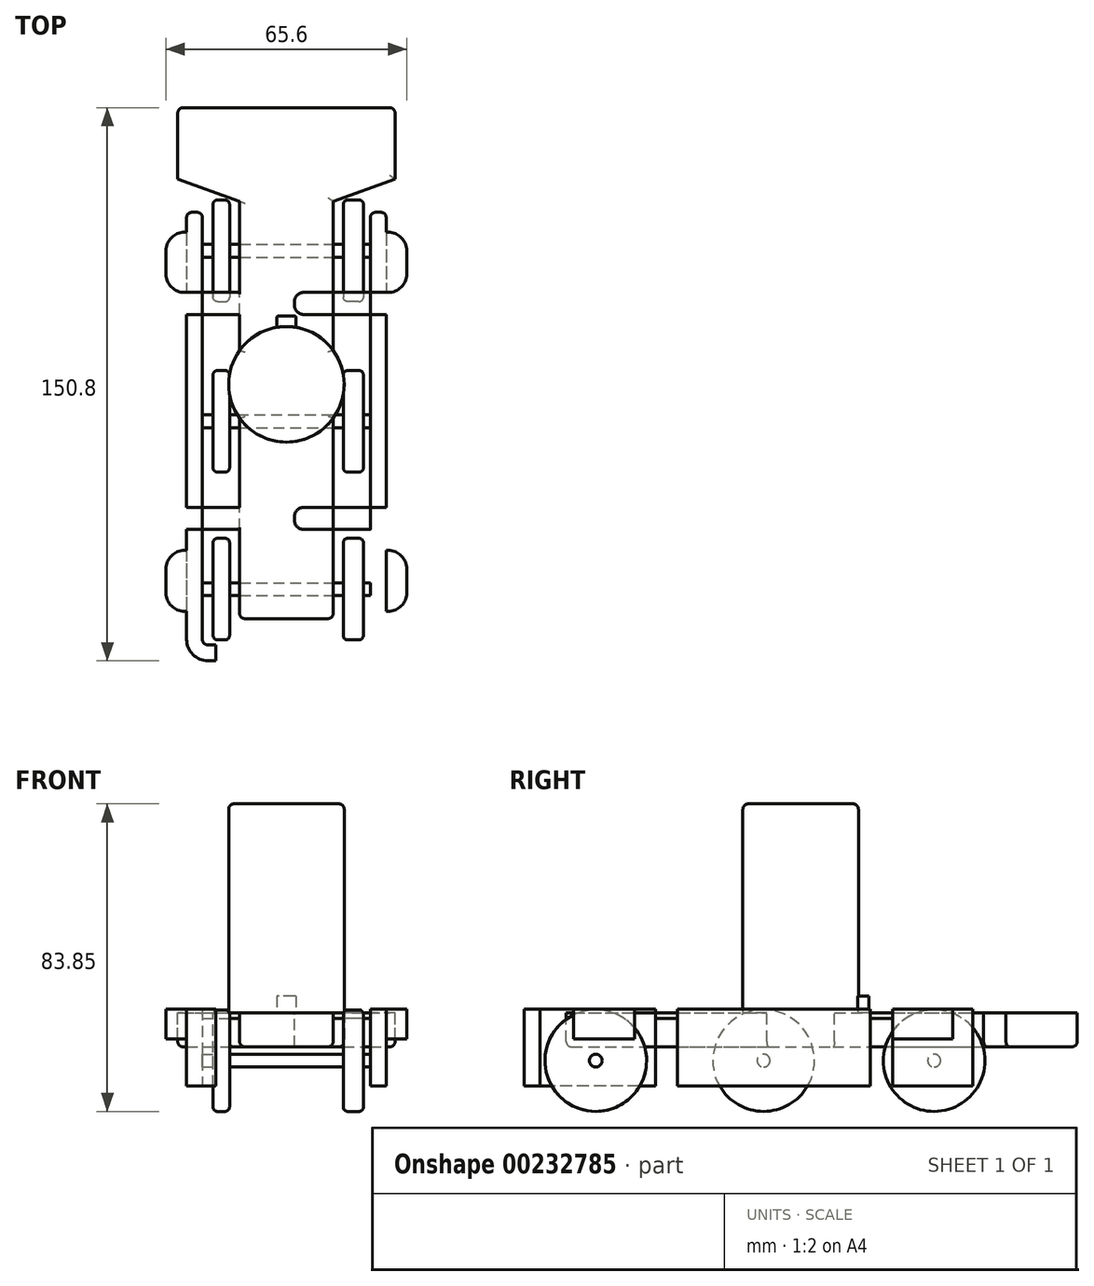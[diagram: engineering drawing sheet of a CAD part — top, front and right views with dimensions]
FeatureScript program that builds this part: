
annotation { "Feature Type Name" : "Feature", "Feature Type Description" : "" }
export const myFeature = defineFeature(function(context is Context, id is Id, definition is map)
    precondition{}
    {
        {
            var Q0;
            Q0=qCreatedBy(makeId("Top.planeOp"),FACE);
            var sketch = newSketch(context, id + "F0", { "sketchPlane" : qUnion([Q0])});
            skLineSegment(sketch, "E0.bottom", {"start": v(0, 75.4) * mm, "end": v(-29.63, 75.4) * mm});
            skLineSegment(sketch, "E0.top", {"start": v(-19.2, -75.4) * mm, "end": v(-21.33, -75.4) * mm});
            skLineSegment(sketch, "E0.right", {"start": v(-27.2, 46.9) * mm, "end": v(-27.2, -69.53) * mm});
            skPoint(sketch, "E0.middle", {"position": v(0, 0) * mm});
            skCircle(sketch, "E1", {"center": v(0, 0) * mm, "radius": 15.75 * mm});
            skLineSegment(sketch, "E2.bottom", {"start": v(2.65, 18.6) * mm, "end": v(-2.65, 18.6) * mm});
            skLineSegment(sketch, "E2.left", {"start": v(2.65, 18.6) * mm, "end": v(2.65, 15.53) * mm});
            skLineSegment(sketch, "E2.right", {"start": v(-2.65, 18.6) * mm, "end": v(-2.65, 15.53) * mm});
            skPoint(sketch, "E2.middle", {"position": v(0, 16.85) * mm});
            skPoint(sketch, "E3.orphan", {"position": v(-2.65, 15.1) * mm});
            skPoint(sketch, "E4.orphan", {"position": v(2.65, 15.1) * mm});
            skLineSegment(sketch, "E5.0", {"start": v(-19.2, -71.1) * mm, "end": v(-21.33, -71.1) * mm});
            skLineSegment(sketch, "E5.1", {"start": v(-22.9, 46.9) * mm, "end": v(-22.9, -69.53) * mm});
            skLineSegment(sketch, "E6", {"start": v(-27.2, 46.9) * mm, "end": v(-22.9, 46.9) * mm});
            skLineSegment(sketch, "E7", {"start": v(-19.2, -71.1) * mm, "end": v(-19.2, -75.4) * mm});
            skPoint(sketch, "E8.visualSharp", {"position": v(-22.9, -71.1) * mm});
            skArc(sketch, "E8.filletArc", {"start": v(-22.9, -69.53) * mm, "mid": v(-22.44, -70.64) * mm, "end": v(-21.33, -71.1) * mm});
            skArc(sketch, "E9.0", {"start": v(-27.2, -69.53) * mm, "mid": v(-25.48, -73.68) * mm, "end": v(-21.33, -75.4) * mm});
            skPoint(sketch, "E10.orphan", {"position": v(-27.2, -75.4) * mm});
            skLineSegment(sketch, "E11.top", {"start": v(-12.75, -63.9) * mm, "end": v(0, -63.9) * mm});
            skLineSegment(sketch, "E12.bottom", {"start": v(-27.2, -39.58) * mm, "end": v(-4.7, -39.58) * mm});
            skLineSegment(sketch, "E12.top", {"start": v(-27.2, -33.58) * mm, "end": v(-4.7, -33.58) * mm});
            skLineSegment(sketch, "E12.left", {"start": v(-27.2, -39.58) * mm, "end": v(-27.2, -33.58) * mm});
            skLineSegment(sketch, "E12.right", {"start": v(-2.2, -37.08) * mm, "end": v(-2.2, -36.08) * mm});
            skPoint(sketch, "E13.visualSharp", {"position": v(-2.2, -33.58) * mm});
            skArc(sketch, "E13.filletArc", {"start": v(-2.2, -36.08) * mm, "mid": v(-2.93, -34.3) * mm, "end": v(-4.7, -33.58) * mm});
            skPoint(sketch, "E14.visualSharp", {"position": v(-2.2, -39.58) * mm});
            skArc(sketch, "E14.filletArc", {"start": v(-4.7, -39.58) * mm, "mid": v(-2.93, -38.84) * mm, "end": v(-2.2, -37.08) * mm});
            skLineSegment(sketch, "E15", {"start": v(-29.63, 56) * mm, "end": v(-12.75, 49.9) * mm});
            skPoint(sketch, "E16", {"position": v(0, 75.4) * mm});
            skPoint(sketch, "E17", {"position": v(0, -63.9) * mm});
            skLineSegment(sketch, "E18", {"start": v(-29.63, 56) * mm, "end": v(-29.63, 75.4) * mm});
            skLineSegment(sketch, "E19", {"start": v(-12.75, -63.9) * mm, "end": v(-12.75, 49.9) * mm});
            skLineSegment(sketch, "E20.bottom", {"start": v(-27.2, 19.04) * mm, "end": v(-4.7, 19.04) * mm});
            skLineSegment(sketch, "E20.top", {"start": v(-27.2, 25.04) * mm, "end": v(-4.7, 25.04) * mm});
            skLineSegment(sketch, "E20.left", {"start": v(-27.2, 19.04) * mm, "end": v(-27.2, 25.04) * mm});
            skLineSegment(sketch, "E20.right", {"start": v(-2.2, 21.54) * mm, "end": v(-2.2, 22.54) * mm});
            skPoint(sketch, "E21.visualSharp", {"position": v(-2.2, 25.04) * mm});
            skArc(sketch, "E21.filletArc", {"start": v(-2.2, 22.54) * mm, "mid": v(-2.93, 24.31) * mm, "end": v(-4.7, 25.04) * mm});
            skPoint(sketch, "E22.visualSharp", {"position": v(-2.2, 19.04) * mm});
            skArc(sketch, "E22.filletArc", {"start": v(-4.7, 19.04) * mm, "mid": v(-2.93, 19.78) * mm, "end": v(-2.2, 21.54) * mm});
            skLineSegment(sketch, "E23.bottom", {"start": v(-32.8, 82.4) * mm, "end": v(32.8, 82.4) * mm, "construction": true});
            skLineSegment(sketch, "E23.top", {"start": v(-32.8, -82.4) * mm, "end": v(32.8, -82.4) * mm, "construction": true});
            skLineSegment(sketch, "E23.right", {"start": v(32.8, 82.4) * mm, "end": v(32.8, -82.4) * mm, "construction": true});
            skLineSegment(sketch, "E24.bottom", {"start": v(-32.8, -45.3) * mm, "end": v(-27.2, -45.3) * mm});
            skLineSegment(sketch, "E24.top", {"start": v(-32.8, -61.9) * mm, "end": v(-27.2, -61.9) * mm});
            skLineSegment(sketch, "E24.left", {"start": v(-32.8, -45.3) * mm, "end": v(-32.8, -61.9) * mm});
            skLineSegment(sketch, "E24.right", {"start": v(-27.2, -45.3) * mm, "end": v(-27.2, -61.9) * mm});
            skLineSegment(sketch, "E25.bottom", {"start": v(-32.8, 25.04) * mm, "end": v(-27.2, 25.04) * mm});
            skLineSegment(sketch, "E25.top", {"start": v(-32.8, 41.44) * mm, "end": v(-27.2, 41.44) * mm});
            skLineSegment(sketch, "E25.left", {"start": v(-32.8, 25.04) * mm, "end": v(-32.8, 41.44) * mm});
            skLineSegment(sketch, "E25.right", {"start": v(-27.2, 25.04) * mm, "end": v(-27.2, 41.44) * mm});
            skArc(sketch, "E26.MirrorCS", {"start": v(2.2, -36.08) * mm, "mid": v(2.93, -34.3) * mm, "end": v(4.7, -33.58) * mm});
            skLineSegment(sketch, "E27.MirrorCS", {"start": v(2.2, -37.08) * mm, "end": v(2.2, -36.08) * mm});
            skArc(sketch, "E28.MirrorCS", {"start": v(4.7, -39.58) * mm, "mid": v(2.93, -38.84) * mm, "end": v(2.2, -37.08) * mm});
            skArc(sketch, "E29.MirrorCS", {"start": v(4.7, 19.04) * mm, "mid": v(2.93, 19.78) * mm, "end": v(2.2, 21.54) * mm});
            skLineSegment(sketch, "E30.MirrorCS", {"start": v(2.2, 21.54) * mm, "end": v(2.2, 22.54) * mm});
            skArc(sketch, "E31.MirrorCS", {"start": v(2.2, 22.54) * mm, "mid": v(2.93, 24.31) * mm, "end": v(4.7, 25.04) * mm});
            skArc(sketch, "E32.MirrorCS", {"start": v(22.9, -69.53) * mm, "mid": v(22.44, -70.64) * mm, "end": v(21.33, -71.1) * mm});
            skLineSegment(sketch, "E33.MirrorCS", {"start": v(19.2, -75.4) * mm, "end": v(21.33, -75.4) * mm});
            skLineSegment(sketch, "E34.MirrorCS", {"start": v(19.2, -71.1) * mm, "end": v(21.33, -71.1) * mm});
            skLineSegment(sketch, "E35.MirrorCS", {"start": v(27.2, -45.3) * mm, "end": v(27.2, -61.9) * mm});
            skLineSegment(sketch, "E36.MirrorCS", {"start": v(32.8, -45.3) * mm, "end": v(32.8, -61.9) * mm});
            skLineSegment(sketch, "E37.MirrorCS", {"start": v(32.8, 25.04) * mm, "end": v(32.8, 41.44) * mm});
            skPoint(sketch, "E38.MirrorP", {"position": v(22.9, -71.1) * mm});
            skLineSegment(sketch, "E39.MirrorCS", {"start": v(27.2, 46.9) * mm, "end": v(27.2, -69.53) * mm});
            skPoint(sketch, "E40.MirrorP", {"position": v(27.2, -75.4) * mm});
            skArc(sketch, "E41.MirrorCS", {"start": v(27.2, -69.53) * mm, "mid": v(25.48, -73.68) * mm, "end": v(21.33, -75.4) * mm});
            skLineSegment(sketch, "E42.MirrorCS", {"start": v(27.2, 46.9) * mm, "end": v(22.9, 46.9) * mm});
            skLineSegment(sketch, "E43.MirrorCS", {"start": v(32.8, -45.3) * mm, "end": v(27.2, -45.3) * mm});
            skLineSegment(sketch, "E44.MirrorCS", {"start": v(27.2, 19.04) * mm, "end": v(27.2, 25.04) * mm});
            skLineSegment(sketch, "E45.MirrorCS", {"start": v(27.2, -39.58) * mm, "end": v(4.7, -39.58) * mm});
            skLineSegment(sketch, "E46.MirrorCS", {"start": v(22.9, 46.9) * mm, "end": v(22.9, -69.53) * mm});
            skLineSegment(sketch, "E47.MirrorCS", {"start": v(32.8, 41.44) * mm, "end": v(27.2, 41.44) * mm});
            skLineSegment(sketch, "E48.MirrorCS", {"start": v(32.8, 25.04) * mm, "end": v(27.2, 25.04) * mm});
            skLineSegment(sketch, "E49.MirrorCS", {"start": v(27.2, 19.04) * mm, "end": v(4.7, 19.04) * mm});
            skLineSegment(sketch, "E50.MirrorCS", {"start": v(27.2, -39.58) * mm, "end": v(27.2, -33.58) * mm});
            skLineSegment(sketch, "E51.MirrorCS", {"start": v(19.2, -71.1) * mm, "end": v(19.2, -75.4) * mm});
            skLineSegment(sketch, "E52.MirrorCS", {"start": v(27.2, -33.58) * mm, "end": v(4.7, -33.58) * mm});
            skLineSegment(sketch, "E53.MirrorCS", {"start": v(32.8, -61.9) * mm, "end": v(27.2, -61.9) * mm});
            skLineSegment(sketch, "E54.MirrorCS", {"start": v(27.2, 25.04) * mm, "end": v(4.7, 25.04) * mm});
            skLineSegment(sketch, "E55.MirrorCS", {"start": v(27.2, 25.04) * mm, "end": v(27.2, 41.44) * mm});
            skLineSegment(sketch, "E56.MirrorCS", {"start": v(12.75, -63.9) * mm, "end": v(0, -63.9) * mm});
            skLineSegment(sketch, "E57.MirrorCS", {"start": v(12.75, -63.9) * mm, "end": v(12.75, 49.9) * mm});
            skLineSegment(sketch, "E58.MirrorCS", {"start": v(29.63, 56) * mm, "end": v(12.75, 49.9) * mm});
            skLineSegment(sketch, "E59.MirrorCS", {"start": v(0, 75.4) * mm, "end": v(29.63, 75.4) * mm});
            skLineSegment(sketch, "E60.MirrorCS", {"start": v(29.63, 56) * mm, "end": v(29.63, 75.4) * mm});
            skSolve(sketch);
        }
        {
            var Q0;
            Q0=makeQuery(id+"F0.imprint","IMPRINT",FACE,{"disambiguationData":[TD([[makeQuery(id+"F0.imprint","IMPRINT",EDGE,{"derivedFrom":sQuery(id+"F0.wireOp",EDGE,"E0.bottom")}),1.0]])]});
            var Q1;
            {var subQ4=sQuery(id+"F0.wireOp",EDGE,"E26.MirrorCS");Q1=makeQuery(id+"F0.imprint","IMPRINT",FACE,{"disambiguationData":[TD([[makeQuery(id+"F0.imprint","IMPRINT",EDGE,{"derivedFrom":subQ4}),-1.0]])]});}
            var Q2;
            {var subQ9=sQuery(id+"F0.wireOp",EDGE,"E11.top");Q2=makeQuery(id+"F0.imprint","IMPRINT",FACE,{"disambiguationData":[TD([[makeQuery(id+"F0.imprint","IMPRINT",EDGE,{"derivedFrom":subQ9}),1.0]])]});}
            var Q3;
            Q3=makeQuery(id+"F0.imprint","IMPRINT",FACE,{"disambiguationData":[TD([[makeQuery(id+"F0.imprint","IMPRINT",EDGE,{"derivedFrom":sQuery(id+"F0.wireOp",EDGE,"E12.right")}),1.0]])]});
            var Q4;
            {var subQ1=sQuery(id+"F0.wireOp",EDGE,"E29.MirrorCS");Q4=makeQuery(id+"F0.imprint","IMPRINT",FACE,{"disambiguationData":[TD([[makeQuery(id+"F0.imprint","IMPRINT",EDGE,{"derivedFrom":subQ1}),-1.0]])]});}
            var Q5;
            Q5=makeQuery(id+"F0.imprint","IMPRINT",FACE,{"disambiguationData":[TD([[makeQuery(id+"F0.imprint","IMPRINT",EDGE,{"derivedFrom":sQuery(id+"F0.wireOp",EDGE,"E20.right")}),1.0]])]});
            extrude(context, id + "F1", {"entities" : qUnion([Q0, Q1, Q2, Q3, Q4, Q5]), "oppositeDirection" : true, "depth" : 7.75 * mm});
        }
        {
            var Q0;
            {var subQ1=sQuery(id+"F0.wireOp",EDGE,"E1");var subQ7=makeQuery(id+"F0.imprint","INTERSECT",VERTEX,{"derivedFrom":[subQ1,sQuery(id+"F0.wireOp",EDGE,"E2.left")]});Q0=makeQuery(id+"F0.imprint","IMPRINT",FACE,{"disambiguationData":[TD([[makeQuery(id+"F0.imprint","IMPRINT",EDGE,{"disambiguationData":[TD([[subQ7,1.0]])],"derivedFrom":subQ1}),1.0]])]});}
            var Q1;
            {var subQ0=sQuery(id+"F0.wireOp",EDGE,"E19");var subQ1=sQuery(id+"F0.wireOp",EDGE,"E1");var subQ2=makeQuery(id+"F0.imprint","INTERSECT",VERTEX,{"disambiguationData":[OD(0.0)],"derivedFrom":[subQ1,subQ0]});Q1=makeQuery(id+"F0.imprint","IMPRINT",FACE,{"disambiguationData":[TD([[makeQuery(id+"F0.imprint","IMPRINT",EDGE,{"disambiguationData":[TD([[subQ2,-1.0]])],"derivedFrom":subQ1}),1.0]])]});}
            var Q2;
            {var subQ0=sQuery(id+"F0.wireOp",EDGE,"E57.MirrorCS");var subQ1=sQuery(id+"F0.wireOp",EDGE,"E1");var subQ2=makeQuery(id+"F0.imprint","INTERSECT",VERTEX,{"disambiguationData":[OD(0.0)],"derivedFrom":[subQ1,subQ0]});Q2=makeQuery(id+"F0.imprint","IMPRINT",FACE,{"disambiguationData":[TD([[makeQuery(id+"F0.imprint","IMPRINT",EDGE,{"disambiguationData":[TD([[subQ2,1.0]])],"derivedFrom":subQ1}),1.0]])]});}
            var Q3;
            Q3=makeQuery(id+"F1.opExtrude","CAP_FACE",FACE,{"disambiguationData":[OSD([sQuery(id+"F0.wireOp",EDGE,"E1"),sQuery(id+"F0.wireOp",EDGE,"E11.top"),sQuery(id+"F0.wireOp",EDGE,"E19"),sQuery(id+"F0.wireOp",EDGE,"E56.MirrorCS"),sQuery(id+"F0.wireOp",EDGE,"E57.MirrorCS")])],"isStart":false});
            extrude(context, id + "F2", {"entities" : qUnion([Q0, Q1, Q2]), "operationType" : NewBodyOperationType.ADD, "depth" : 58.5 * mm, "hasSecondDirection" : true, "secondDirectionBound" : SecondDirectionBoundingType.UP_TO_SURFACE, "secondDirectionOppositeDirection" : true, "secondDirectionBoundEntityFace" : qUnion([Q3]), "secondDirectionDepth" : 25 * mm});
        }
        {
            var Q0;
            Q0=makeQuery(id+"F0.imprint","IMPRINT",FACE,{"disambiguationData":[TD([[makeQuery(id+"F0.imprint","IMPRINT",EDGE,{"derivedFrom":sQuery(id+"F0.wireOp",EDGE,"E2.bottom")}),1.0]])]});
            var Q1;
            Q1=makeQuery(id+"F1.opExtrude","CAP_FACE",FACE,{"disambiguationData":[OSD([sQuery(id+"F0.wireOp",EDGE,"E0.bottom"),sQuery(id+"F0.wireOp",EDGE,"E1"),sQuery(id+"F0.wireOp",EDGE,"E2.bottom"),sQuery(id+"F0.wireOp",EDGE,"E2.left"),sQuery(id+"F0.wireOp",EDGE,"E2.right"),sQuery(id+"F0.wireOp",EDGE,"E15"),sQuery(id+"F0.wireOp",EDGE,"E18"),sQuery(id+"F0.wireOp",EDGE,"E19"),sQuery(id+"F0.wireOp",EDGE,"E57.MirrorCS"),sQuery(id+"F0.wireOp",EDGE,"E58.MirrorCS"),sQuery(id+"F0.wireOp",EDGE,"E59.MirrorCS"),sQuery(id+"F0.wireOp",EDGE,"E60.MirrorCS")])],"isStart":false});
            extrude(context, id + "F3", {"entities" : qUnion([Q0]), "operationType" : NewBodyOperationType.ADD, "depth" : 6.1 * mm, "hasSecondDirection" : true, "secondDirectionBound" : SecondDirectionBoundingType.UP_TO_SURFACE, "secondDirectionOppositeDirection" : true, "secondDirectionBoundEntityFace" : qUnion([Q1]), "secondDirectionDepth" : 25 * mm});
        }
        {
            var Q0;
            {var subQ7=sQuery(id+"F0.wireOp",EDGE,"E32.MirrorCS");Q0=makeQuery(id+"F0.imprint","IMPRINT",FACE,{"disambiguationData":[TD([[makeQuery(id+"F0.imprint","IMPRINT",EDGE,{"derivedFrom":subQ7}),1.0]])]});}
            var Q1;
            {var subQ0=sQuery(id+"F0.wireOp",EDGE,"E50.MirrorCS");Q1=makeQuery(id+"F0.imprint","IMPRINT",FACE,{"disambiguationData":[TD([[makeQuery(id+"F0.imprint","IMPRINT",EDGE,{"derivedFrom":subQ0}),1.0]])]});}
            var Q2;
            {var subQ0=sQuery(id+"F0.wireOp",EDGE,"E49.MirrorCS");var subQ5=sQuery(id+"F0.wireOp",EDGE,"E46.MirrorCS");var subQ6=makeQuery(id+"F0.imprint","INTERSECT",VERTEX,{"derivedFrom":[subQ5,subQ0]});Q2=makeQuery(id+"F0.imprint","IMPRINT",FACE,{"disambiguationData":[TD([[makeQuery(id+"F0.imprint","IMPRINT",EDGE,{"disambiguationData":[TD([[subQ6,-1.0]])],"derivedFrom":subQ5}),1.0]])]});}
            var Q3;
            {var subQ5=sQuery(id+"F0.wireOp",EDGE,"E44.MirrorCS");Q3=makeQuery(id+"F0.imprint","IMPRINT",FACE,{"disambiguationData":[TD([[makeQuery(id+"F0.imprint","IMPRINT",EDGE,{"derivedFrom":subQ5}),1.0]])]});}
            var Q4;
            {var subQ7=sQuery(id+"F0.wireOp",EDGE,"E42.MirrorCS");Q4=makeQuery(id+"F0.imprint","IMPRINT",FACE,{"disambiguationData":[TD([[makeQuery(id+"F0.imprint","IMPRINT",EDGE,{"derivedFrom":subQ7}),1.0]])]});}
            var Q5;
            {var subQ0=sQuery(id+"F0.wireOp",EDGE,"E6");Q5=makeQuery(id+"F0.imprint","IMPRINT",FACE,{"disambiguationData":[TD([[makeQuery(id+"F0.imprint","IMPRINT",EDGE,{"derivedFrom":subQ0}),-1.0]])]});}
            var Q6;
            {var subQ3=sQuery(id+"F0.wireOp",EDGE,"E20.bottom");var subQ5=sQuery(id+"F0.wireOp",EDGE,"E5.1");var subQ6=makeQuery(id+"F0.imprint","INTERSECT",VERTEX,{"derivedFrom":[subQ5,subQ3]});Q6=makeQuery(id+"F0.imprint","IMPRINT",FACE,{"disambiguationData":[TD([[makeQuery(id+"F0.imprint","IMPRINT",EDGE,{"disambiguationData":[TD([[subQ6,-1.0]])],"derivedFrom":subQ5}),-1.0]])]});}
            var Q7;
            {var subQ0=sQuery(id+"F0.wireOp",EDGE,"E20.left");Q7=makeQuery(id+"F0.imprint","IMPRINT",FACE,{"disambiguationData":[TD([[makeQuery(id+"F0.imprint","IMPRINT",EDGE,{"derivedFrom":subQ0}),-1.0]])]});}
            var Q8;
            {var subQ5=sQuery(id+"F0.wireOp",EDGE,"E12.left");Q8=makeQuery(id+"F0.imprint","IMPRINT",FACE,{"disambiguationData":[TD([[makeQuery(id+"F0.imprint","IMPRINT",EDGE,{"derivedFrom":subQ5}),-1.0]])]});}
            var Q9;
            Q9=makeQuery(id+"F0.imprint","IMPRINT",FACE,{"disambiguationData":[TD([[makeQuery(id+"F0.imprint","IMPRINT",EDGE,{"derivedFrom":sQuery(id+"F0.wireOp",EDGE,"E0.top")}),-1.0]])]});
            extrude(context, id + "F4", {"entities" : qUnion([Q0, Q1, Q2, Q3, Q4, Q5, Q6, Q7, Q8, Q9]), "operationType" : NewBodyOperationType.ADD, "depth" : 2.54 * mm, "hasSecondDirection" : true, "secondDirectionOppositeDirection" : true, "secondDirectionDepth" : 18.46 * mm});
        }
        {
            var Q0;
            Q0=makeQuery(id+"F0.imprint","IMPRINT",FACE,{"disambiguationData":[TD([[makeQuery(id+"F0.imprint","IMPRINT",EDGE,{"derivedFrom":sQuery(id+"F0.wireOp",EDGE,"E37.MirrorCS")}),1.0]])]});
            var Q1;
            Q1=makeQuery(id+"F0.imprint","IMPRINT",FACE,{"disambiguationData":[TD([[makeQuery(id+"F0.imprint","IMPRINT",EDGE,{"derivedFrom":sQuery(id+"F0.wireOp",EDGE,"E36.MirrorCS")}),-1.0]])]});
            var Q2;
            Q2=makeQuery(id+"F0.imprint","IMPRINT",FACE,{"disambiguationData":[TD([[makeQuery(id+"F0.imprint","IMPRINT",EDGE,{"derivedFrom":sQuery(id+"F0.wireOp",EDGE,"E24.bottom")}),-1.0]])]});
            var Q3;
            {var subQ2=sQuery(id+"F0.wireOp",EDGE,"E25.bottom");Q3=makeQuery(id+"F0.imprint","IMPRINT",FACE,{"disambiguationData":[TD([[makeQuery(id+"F0.imprint","IMPRINT",EDGE,{"derivedFrom":subQ2}),1.0]])]});}
            var Q4;
            Q4=makeQuery(id+"F4.opExtrude","CAP_FACE",FACE,{"disambiguationData":[OSD([sQuery(id+"F0.wireOp",EDGE,"E32.MirrorCS"),sQuery(id+"F0.wireOp",EDGE,"E33.MirrorCS"),sQuery(id+"F0.wireOp",EDGE,"E34.MirrorCS"),sQuery(id+"F0.wireOp",EDGE,"E39.MirrorCS"),sQuery(id+"F0.wireOp",EDGE,"E41.MirrorCS"),sQuery(id+"F0.wireOp",EDGE,"E42.MirrorCS"),sQuery(id+"F0.wireOp",EDGE,"E44.MirrorCS"),sQuery(id+"F0.wireOp",EDGE,"E46.MirrorCS"),sQuery(id+"F0.wireOp",EDGE,"E50.MirrorCS"),sQuery(id+"F0.wireOp",EDGE,"E51.MirrorCS"),sQuery(id+"F0.wireOp",EDGE,"E55.MirrorCS")])],"isStart":false});
            extrude(context, id + "F5", {"entities" : qUnion([Q0, Q1, Q2, Q3]), "operationType" : NewBodyOperationType.ADD, "endBound" : BoundingType.UP_TO_SURFACE, "endBoundEntityFace" : qUnion([Q4]), "depth" : 5.6 * mm, "hasSecondDirection" : true, "secondDirectionOppositeDirection" : true, "secondDirectionDepth" : 5.6 * mm});
        }
        {
            var Q0;
            {var subQ0=sQuery(id+"F0.wireOp",EDGE,"E12.bottom");var subQ1=sQuery(id+"F0.wireOp",EDGE,"E5.1");var subQ2=makeQuery(id+"F0.imprint","INTERSECT",VERTEX,{"derivedFrom":[subQ1,subQ0]});Q0=makeQuery(id+"F0.imprint","IMPRINT",FACE,{"disambiguationData":[TD([[makeQuery(id+"F0.imprint","IMPRINT",EDGE,{"disambiguationData":[TD([[subQ2,1.0]])],"derivedFrom":subQ1}),1.0]])]});}
            var Q1;
            Q1=makeQuery(id+"F0.imprint","IMPRINT",FACE,{"disambiguationData":[TD([[makeQuery(id+"F0.imprint","IMPRINT",EDGE,{"derivedFrom":sQuery(id+"F0.wireOp",EDGE,"E12.right")}),1.0]])]});
            var Q2;
            {var subQ4=sQuery(id+"F0.wireOp",EDGE,"E26.MirrorCS");Q2=makeQuery(id+"F0.imprint","IMPRINT",FACE,{"disambiguationData":[TD([[makeQuery(id+"F0.imprint","IMPRINT",EDGE,{"derivedFrom":subQ4}),-1.0]])]});}
            var Q3;
            {var subQ0=sQuery(id+"F0.wireOp",EDGE,"E46.MirrorCS");var subQ1=sQuery(id+"F0.wireOp",EDGE,"E45.MirrorCS");var subQ2=makeQuery(id+"F0.imprint","INTERSECT",VERTEX,{"derivedFrom":[subQ1,subQ0]});Q3=makeQuery(id+"F0.imprint","IMPRINT",FACE,{"disambiguationData":[TD([[makeQuery(id+"F0.imprint","IMPRINT",EDGE,{"disambiguationData":[TD([[subQ2,-1.0]])],"derivedFrom":subQ1}),-1.0]])]});}
            var Q4;
            {var subQ0=sQuery(id+"F0.wireOp",EDGE,"E54.MirrorCS");var subQ1=sQuery(id+"F0.wireOp",EDGE,"E46.MirrorCS");var subQ2=makeQuery(id+"F0.imprint","INTERSECT",VERTEX,{"derivedFrom":[subQ1,subQ0]});Q4=makeQuery(id+"F0.imprint","IMPRINT",FACE,{"disambiguationData":[TD([[makeQuery(id+"F0.imprint","IMPRINT",EDGE,{"disambiguationData":[TD([[subQ2,-1.0]])],"derivedFrom":subQ1}),-1.0]])]});}
            var Q5;
            {var subQ1=sQuery(id+"F0.wireOp",EDGE,"E29.MirrorCS");Q5=makeQuery(id+"F0.imprint","IMPRINT",FACE,{"disambiguationData":[TD([[makeQuery(id+"F0.imprint","IMPRINT",EDGE,{"derivedFrom":subQ1}),-1.0]])]});}
            var Q6;
            Q6=makeQuery(id+"F0.imprint","IMPRINT",FACE,{"disambiguationData":[TD([[makeQuery(id+"F0.imprint","IMPRINT",EDGE,{"derivedFrom":sQuery(id+"F0.wireOp",EDGE,"E20.right")}),1.0]])]});
            var Q7;
            {var subQ0=sQuery(id+"F0.wireOp",EDGE,"E20.top");var subQ1=sQuery(id+"F0.wireOp",EDGE,"E5.1");var subQ2=makeQuery(id+"F0.imprint","INTERSECT",VERTEX,{"derivedFrom":[subQ1,subQ0]});Q7=makeQuery(id+"F0.imprint","IMPRINT",FACE,{"disambiguationData":[TD([[makeQuery(id+"F0.imprint","IMPRINT",EDGE,{"disambiguationData":[TD([[subQ2,-1.0]])],"derivedFrom":subQ1}),1.0]])]});}
            var Q8;
            {var subQ0=sQuery(id+"F0.wireOp",EDGE,"E55.MirrorCS");var subQ1=sQuery(id+"F0.wireOp",EDGE,"E39.MirrorCS");Q8=makeQuery(id+"F5.boolean.opBoolean","MERGE",FACE,{"derivedFrom":[makeQuery(id+"F4.opExtrude","CAP_FACE",FACE,{"disambiguationData":[OSD([sQuery(id+"F0.wireOp",EDGE,"E32.MirrorCS"),sQuery(id+"F0.wireOp",EDGE,"E33.MirrorCS"),sQuery(id+"F0.wireOp",EDGE,"E34.MirrorCS"),subQ1,sQuery(id+"F0.wireOp",EDGE,"E41.MirrorCS"),sQuery(id+"F0.wireOp",EDGE,"E42.MirrorCS"),sQuery(id+"F0.wireOp",EDGE,"E44.MirrorCS"),sQuery(id+"F0.wireOp",EDGE,"E46.MirrorCS"),sQuery(id+"F0.wireOp",EDGE,"E50.MirrorCS"),sQuery(id+"F0.wireOp",EDGE,"E51.MirrorCS"),subQ0])],"isStart":false}),makeQuery(id+"F5.opExtrude","CAP_FACE",FACE,{"disambiguationData":[OSD([sQuery(id+"F0.wireOp",EDGE,"E36.MirrorCS"),subQ1,sQuery(id+"F0.wireOp",EDGE,"E43.MirrorCS"),sQuery(id+"F0.wireOp",EDGE,"E53.MirrorCS")])],"isStart":false}),makeQuery(id+"F5.opExtrude","CAP_FACE",FACE,{"disambiguationData":[OSD([sQuery(id+"F0.wireOp",EDGE,"E37.MirrorCS"),sQuery(id+"F0.wireOp",EDGE,"E47.MirrorCS"),sQuery(id+"F0.wireOp",EDGE,"E48.MirrorCS"),subQ0])],"isStart":false})]});}
            var Q9;
            Q9=makeQuery(id+"F1.opExtrude","CAP_FACE",FACE,{"disambiguationData":[OSD([sQuery(id+"F0.wireOp",EDGE,"E1"),sQuery(id+"F0.wireOp",EDGE,"E11.top"),sQuery(id+"F0.wireOp",EDGE,"E19"),sQuery(id+"F0.wireOp",EDGE,"E56.MirrorCS"),sQuery(id+"F0.wireOp",EDGE,"E57.MirrorCS")])],"isStart":true});
            extrude(context, id + "F6", {"entities" : qUnion([Q0, Q1, Q2, Q3, Q4, Q5, Q6, Q7]), "operationType" : NewBodyOperationType.ADD, "endBoundEntityFace" : qUnion([Q8]), "depth" : 1.5 * mm});
        }
        {
            var Q0;
            Q0=makeQuery(id+"F5.opExtrude","SWEPT_EDGE",EDGE,{"disambiguationData":[OSD([sQuery(id+"F0.wireOp",EDGE,"E36.MirrorCS"),sQuery(id+"F0.wireOp",EDGE,"E53.MirrorCS")])]});
            var Q1;
            Q1=makeQuery(id+"F5.opExtrude","SWEPT_EDGE",EDGE,{"disambiguationData":[OSD([sQuery(id+"F0.wireOp",EDGE,"E36.MirrorCS"),sQuery(id+"F0.wireOp",EDGE,"E43.MirrorCS")])]});
            var Q2;
            Q2=makeQuery(id+"F5.opExtrude","SWEPT_EDGE",EDGE,{"disambiguationData":[OSD([sQuery(id+"F0.wireOp",EDGE,"E37.MirrorCS"),sQuery(id+"F0.wireOp",EDGE,"E48.MirrorCS")])]});
            var Q3;
            Q3=makeQuery(id+"F5.opExtrude","SWEPT_EDGE",EDGE,{"disambiguationData":[OSD([sQuery(id+"F0.wireOp",EDGE,"E37.MirrorCS"),sQuery(id+"F0.wireOp",EDGE,"E47.MirrorCS")])]});
            var Q4;
            Q4=makeQuery(id+"F5.opExtrude","SWEPT_EDGE",EDGE,{"disambiguationData":[OSD([sQuery(id+"F0.wireOp",EDGE,"E24.top"),sQuery(id+"F0.wireOp",EDGE,"E24.left")])]});
            var Q5;
            Q5=makeQuery(id+"F5.opExtrude","SWEPT_EDGE",EDGE,{"disambiguationData":[OSD([sQuery(id+"F0.wireOp",EDGE,"E24.bottom"),sQuery(id+"F0.wireOp",EDGE,"E24.left")])]});
            var Q6;
            Q6=makeQuery(id+"F5.opExtrude","SWEPT_EDGE",EDGE,{"disambiguationData":[OSD([sQuery(id+"F0.wireOp",EDGE,"E25.bottom"),sQuery(id+"F0.wireOp",EDGE,"E25.left")])]});
            var Q7;
            Q7=makeQuery(id+"F5.opExtrude","SWEPT_EDGE",EDGE,{"disambiguationData":[OSD([sQuery(id+"F0.wireOp",EDGE,"E25.top"),sQuery(id+"F0.wireOp",EDGE,"E25.left")])]});
            fillet(context, id + "F7", {"entities" : qUnion([Q0, Q1, Q2, Q3, Q4, Q5, Q6, Q7]), "radius" : 5 * mm, "tangentPropagation" : true, "allowEdgeOverflow" : false});
        }
        {
            var Q0;
            Q0=makeQuery(id+"F6.opExtrude","CAP_EDGE",EDGE,{"disambiguationData":[OSD([sQuery(id+"F0.wireOp",EDGE,"E45.MirrorCS")])],"isStart":false});
            var Q1;
            Q1=makeQuery(id+"F6.opExtrude","CAP_EDGE",EDGE,{"disambiguationData":[OSD([sQuery(id+"F0.wireOp",EDGE,"E12.bottom")])],"isStart":false});
            var Q2;
            Q2=makeQuery(id+"F6.opExtrude","CAP_EDGE",EDGE,{"disambiguationData":[OSD([sQuery(id+"F0.wireOp",EDGE,"E54.MirrorCS")])],"isStart":false});
            var Q3;
            Q3=makeQuery(id+"F6.opExtrude","CAP_EDGE",EDGE,{"disambiguationData":[OSD([sQuery(id+"F0.wireOp",EDGE,"E20.top")])],"isStart":false});
            var Q4;
            Q4=makeQuery(id+"F3.opExtrude","SWEPT_EDGE",EDGE,{"disambiguationData":[OSD([sQuery(id+"F0.wireOp",EDGE,"E2.bottom"),sQuery(id+"F0.wireOp",EDGE,"E2.right")])]});
            var Q5;
            Q5=makeQuery(id+"F3.opExtrude","SWEPT_EDGE",EDGE,{"disambiguationData":[OSD([sQuery(id+"F0.wireOp",EDGE,"E2.bottom"),sQuery(id+"F0.wireOp",EDGE,"E2.left")])]});
            fillet(context, id + "F8", {"entities" : qUnion([Q0, Q1, Q2, Q3, Q4, Q5]), "radius" : 0.48 * mm, "tangentPropagation" : true, "allowEdgeOverflow" : false});
        }
        {
            var Q0;
            Q0=makeQuery(id+"F4.opExtrude","SWEPT_EDGE",EDGE,{"disambiguationData":[OSD([sQuery(id+"F0.wireOp",EDGE,"E0.right"),sQuery(id+"F0.wireOp",EDGE,"E6")])]});
            var Q1;
            Q1=makeQuery(id+"F4.opExtrude","SWEPT_EDGE",EDGE,{"disambiguationData":[OSD([sQuery(id+"F0.wireOp",EDGE,"E5.1"),sQuery(id+"F0.wireOp",EDGE,"E6")])]});
            var Q2;
            Q2=makeQuery(id+"F4.opExtrude","SWEPT_EDGE",EDGE,{"disambiguationData":[OSD([sQuery(id+"F0.wireOp",EDGE,"E39.MirrorCS"),sQuery(id+"F0.wireOp",EDGE,"E42.MirrorCS")])]});
            var Q3;
            Q3=makeQuery(id+"F4.opExtrude","SWEPT_EDGE",EDGE,{"disambiguationData":[OSD([sQuery(id+"F0.wireOp",EDGE,"E42.MirrorCS"),sQuery(id+"F0.wireOp",EDGE,"E46.MirrorCS")])]});
            var Q4;
            Q4=makeQuery(id+"F1.opExtrude","SWEPT_EDGE",EDGE,{"disambiguationData":[OSD([sQuery(id+"F0.wireOp",EDGE,"E56.MirrorCS"),sQuery(id+"F0.wireOp",EDGE,"E57.MirrorCS")])]});
            var Q5;
            Q5=makeQuery(id+"F1.opExtrude","SWEPT_EDGE",EDGE,{"disambiguationData":[OSD([sQuery(id+"F0.wireOp",EDGE,"E11.top"),sQuery(id+"F0.wireOp",EDGE,"E19")])]});
            var Q6;
            {var subQ1=sQuery(id+"F0.wireOp",EDGE,"E12.bottom");var subQ2=sQuery(id+"F0.wireOp",EDGE,"E19");var subQ3=sQuery(id+"F0.wireOp",EDGE,"E1");var subQ5=makeQuery(id+"F0.imprint","IMPRINT",EDGE,{"disambiguationData":[TD([[makeQuery(id+"F0.imprint","INTERSECT",VERTEX,{"disambiguationData":[OD(1.0)],"derivedFrom":[subQ3,subQ2]}),1.0]])],"derivedFrom":subQ2});var subQ6=makeQuery(id+"F0.imprint","INTERSECT",VERTEX,{"derivedFrom":[subQ1,subQ2]});var subQ7=makeQuery(id+"F0.imprint","IMPRINT",EDGE,{"disambiguationData":[TD([[subQ6,-1.0]])],"derivedFrom":subQ2});var subQ8=sQuery(id+"F0.wireOp",EDGE,"E11.top");var subQ9=makeQuery(id+"F0.imprint","IMPRINT",EDGE,{"disambiguationData":[TD([[makeQuery(id+"F0.imprint","INTERSECT",VERTEX,{"derivedFrom":[subQ8,subQ2]}),-1.0]])],"derivedFrom":subQ2});var subQ10=makeQuery(id+"F1.opExtrude","SWEPT_FACE",FACE,{"disambiguationData":[OSD([subQ2]),TDD([subQ9,subQ7,subQ5])]});var subQ11=makeQuery(id+"F1.opExtrude","CAP_FACE",FACE,{"disambiguationData":[OSD([subQ3,subQ8,subQ2,sQuery(id+"F0.wireOp",EDGE,"E56.MirrorCS"),sQuery(id+"F0.wireOp",EDGE,"E57.MirrorCS")])],"isStart":true});Q6=makeQuery(id+"F6.boolean.opBoolean","SPLIT",EDGE,{"disambiguationData":[topologyDisambiguationEdgeConnected([subQ11,subQ10]),TD([makeQuery(id+"F2.opExtrude","SWEPT_FACE",FACE,{"disambiguationData":[OSD([subQ3])]})])],"derivedFrom":makeQuery(id+"F1.opExtrude","CAP_EDGE",EDGE,{"disambiguationData":[OSD([subQ2]),TDD([subQ9,subQ7,subQ5])],"isStart":true})});}
            var Q7;
            {var subQ0=sQuery(id+"F0.wireOp",EDGE,"E12.top");var subQ1=sQuery(id+"F0.wireOp",EDGE,"E12.bottom");var subQ2=sQuery(id+"F0.wireOp",EDGE,"E19");var subQ3=sQuery(id+"F0.wireOp",EDGE,"E1");var subQ5=makeQuery(id+"F0.imprint","IMPRINT",EDGE,{"disambiguationData":[TD([[makeQuery(id+"F0.imprint","INTERSECT",VERTEX,{"disambiguationData":[OD(1.0)],"derivedFrom":[subQ3,subQ2]}),1.0]])],"derivedFrom":subQ2});var subQ6=makeQuery(id+"F0.imprint","INTERSECT",VERTEX,{"derivedFrom":[subQ1,subQ2]});var subQ7=makeQuery(id+"F0.imprint","IMPRINT",EDGE,{"disambiguationData":[TD([[subQ6,-1.0]])],"derivedFrom":subQ2});var subQ8=sQuery(id+"F0.wireOp",EDGE,"E11.top");var subQ9=makeQuery(id+"F0.imprint","IMPRINT",EDGE,{"disambiguationData":[TD([[makeQuery(id+"F0.imprint","INTERSECT",VERTEX,{"derivedFrom":[subQ8,subQ2]}),-1.0]])],"derivedFrom":subQ2});var subQ10=sQuery(id+"F0.wireOp",EDGE,"E56.MirrorCS");Q7=makeQuery(id+"F6.boolean.opBoolean","SPLIT",EDGE,{"disambiguationData":[TD([makeQuery(id+"F1.opExtrude","CAP_FACE",FACE,{"disambiguationData":[OSD([subQ3,subQ8,subQ2,subQ10,sQuery(id+"F0.wireOp",EDGE,"E57.MirrorCS")])],"isStart":true}),makeQuery(id+"F1.opExtrude","SWEPT_FACE",FACE,{"disambiguationData":[OSD([subQ8,subQ10])]}),makeQuery(id+"F1.opExtrude","SWEPT_FACE",FACE,{"disambiguationData":[OSD([subQ2]),TDD([subQ9,subQ7,subQ5])]}),makeQuery(id+"F6.opExtrude","CAP_FACE",FACE,{"disambiguationData":[OSD([sQuery(id+"F0.wireOp",EDGE,"E5.1"),subQ1,subQ0,sQuery(id+"F0.wireOp",EDGE,"E12.right"),sQuery(id+"F0.wireOp",EDGE,"E13.filletArc"),sQuery(id+"F0.wireOp",EDGE,"E14.filletArc")])],"isStart":true}),makeQuery(id+"F6.opExtrude","SWEPT_FACE",FACE,{"disambiguationData":[OSD([subQ1])]})])],"derivedFrom":makeQuery(id+"F1.opExtrude","CAP_EDGE",EDGE,{"disambiguationData":[OSD([subQ2]),TDD([subQ9,subQ7,subQ5])],"isStart":true})});}
            var Q8;
            {var subQ0=sQuery(id+"F0.wireOp",EDGE,"E57.MirrorCS");var subQ1=sQuery(id+"F0.wireOp",EDGE,"E1");var subQ2=sQuery(id+"F0.wireOp",EDGE,"E52.MirrorCS");var subQ4=makeQuery(id+"F0.imprint","IMPRINT",EDGE,{"disambiguationData":[TD([[makeQuery(id+"F0.imprint","INTERSECT",VERTEX,{"disambiguationData":[OD(1.0)],"derivedFrom":[subQ1,subQ0]}),1.0]])],"derivedFrom":subQ0});var subQ5=sQuery(id+"F0.wireOp",EDGE,"E45.MirrorCS");var subQ6=makeQuery(id+"F0.imprint","INTERSECT",VERTEX,{"derivedFrom":[subQ5,subQ0]});var subQ7=makeQuery(id+"F0.imprint","IMPRINT",EDGE,{"disambiguationData":[TD([[subQ6,-1.0]])],"derivedFrom":subQ0});var subQ8=sQuery(id+"F0.wireOp",EDGE,"E56.MirrorCS");var subQ9=makeQuery(id+"F0.imprint","IMPRINT",EDGE,{"disambiguationData":[TD([[makeQuery(id+"F0.imprint","INTERSECT",VERTEX,{"derivedFrom":[subQ8,subQ0]}),-1.0]])],"derivedFrom":subQ0});var subQ10=sQuery(id+"F0.wireOp",EDGE,"E11.top");Q8=makeQuery(id+"F6.boolean.opBoolean","SPLIT",EDGE,{"disambiguationData":[TD([makeQuery(id+"F1.opExtrude","CAP_FACE",FACE,{"disambiguationData":[OSD([subQ1,subQ10,sQuery(id+"F0.wireOp",EDGE,"E19"),subQ8,subQ0])],"isStart":true}),makeQuery(id+"F1.opExtrude","SWEPT_FACE",FACE,{"disambiguationData":[OSD([subQ10,subQ8])]}),makeQuery(id+"F1.opExtrude","SWEPT_FACE",FACE,{"disambiguationData":[OSD([subQ0]),TDD([subQ9,subQ7,subQ4])]}),makeQuery(id+"F6.opExtrude","CAP_FACE",FACE,{"disambiguationData":[OSD([sQuery(id+"F0.wireOp",EDGE,"E26.MirrorCS"),sQuery(id+"F0.wireOp",EDGE,"E27.MirrorCS"),sQuery(id+"F0.wireOp",EDGE,"E28.MirrorCS"),subQ5,sQuery(id+"F0.wireOp",EDGE,"E46.MirrorCS"),subQ2])],"isStart":true}),makeQuery(id+"F6.opExtrude","SWEPT_FACE",FACE,{"disambiguationData":[OSD([subQ5])]})])],"derivedFrom":makeQuery(id+"F1.opExtrude","CAP_EDGE",EDGE,{"disambiguationData":[OSD([subQ0]),TDD([subQ9,subQ7,subQ4])],"isStart":true})});}
            var Q9;
            {var subQ1=sQuery(id+"F0.wireOp",EDGE,"E45.MirrorCS");var subQ2=sQuery(id+"F0.wireOp",EDGE,"E1");var subQ3=sQuery(id+"F0.wireOp",EDGE,"E57.MirrorCS");var subQ5=makeQuery(id+"F0.imprint","IMPRINT",EDGE,{"disambiguationData":[TD([[makeQuery(id+"F0.imprint","INTERSECT",VERTEX,{"disambiguationData":[OD(1.0)],"derivedFrom":[subQ2,subQ3]}),1.0]])],"derivedFrom":subQ3});var subQ6=makeQuery(id+"F0.imprint","INTERSECT",VERTEX,{"derivedFrom":[subQ1,subQ3]});var subQ7=makeQuery(id+"F0.imprint","IMPRINT",EDGE,{"disambiguationData":[TD([[subQ6,-1.0]])],"derivedFrom":subQ3});var subQ8=sQuery(id+"F0.wireOp",EDGE,"E56.MirrorCS");var subQ9=makeQuery(id+"F0.imprint","IMPRINT",EDGE,{"disambiguationData":[TD([[makeQuery(id+"F0.imprint","INTERSECT",VERTEX,{"derivedFrom":[subQ8,subQ3]}),-1.0]])],"derivedFrom":subQ3});var subQ10=makeQuery(id+"F1.opExtrude","SWEPT_FACE",FACE,{"disambiguationData":[OSD([subQ3]),TDD([subQ9,subQ7,subQ5])]});var subQ11=makeQuery(id+"F1.opExtrude","CAP_FACE",FACE,{"disambiguationData":[OSD([subQ2,sQuery(id+"F0.wireOp",EDGE,"E11.top"),sQuery(id+"F0.wireOp",EDGE,"E19"),subQ8,subQ3])],"isStart":true});Q9=makeQuery(id+"F6.boolean.opBoolean","SPLIT",EDGE,{"disambiguationData":[topologyDisambiguationEdgeConnected([subQ11,subQ10]),TD([makeQuery(id+"F2.opExtrude","SWEPT_FACE",FACE,{"disambiguationData":[OSD([subQ2])]})])],"derivedFrom":makeQuery(id+"F1.opExtrude","CAP_EDGE",EDGE,{"disambiguationData":[OSD([subQ3]),TDD([subQ9,subQ7,subQ5])],"isStart":true})});}
            var Q10;
            Q10=makeQuery(id+"F1.opExtrude","CAP_EDGE",EDGE,{"disambiguationData":[OSD([sQuery(id+"F0.wireOp",EDGE,"E11.top"),sQuery(id+"F0.wireOp",EDGE,"E56.MirrorCS")])],"isStart":true});
            var Q11;
            Q11=makeQuery(id+"F1.opExtrude","CAP_EDGE",EDGE,{"disambiguationData":[OSD([sQuery(id+"F0.wireOp",EDGE,"E11.top"),sQuery(id+"F0.wireOp",EDGE,"E56.MirrorCS")])],"isStart":false});
            var Q12;
            Q12=makeQuery(id+"F1.opExtrude","CAP_EDGE",EDGE,{"disambiguationData":[OSD([sQuery(id+"F0.wireOp",EDGE,"E0.bottom"),sQuery(id+"F0.wireOp",EDGE,"E59.MirrorCS")])],"isStart":true});
            var Q13;
            Q13=makeQuery(id+"F1.opExtrude","CAP_EDGE",EDGE,{"disambiguationData":[OSD([sQuery(id+"F0.wireOp",EDGE,"E60.MirrorCS")])],"isStart":true});
            var Q14;
            Q14=makeQuery(id+"F1.opExtrude","CAP_EDGE",EDGE,{"disambiguationData":[OSD([sQuery(id+"F0.wireOp",EDGE,"E58.MirrorCS")])],"isStart":true});
            var Q15;
            {var subQ0=sQuery(id+"F0.wireOp",EDGE,"E54.MirrorCS");var subQ1=sQuery(id+"F0.wireOp",EDGE,"E49.MirrorCS");var subQ2=sQuery(id+"F0.wireOp",EDGE,"E58.MirrorCS");var subQ3=sQuery(id+"F0.wireOp",EDGE,"E57.MirrorCS");var subQ4=makeQuery(id+"F0.imprint","INTERSECT",VERTEX,{"derivedFrom":[subQ0,subQ3]});var subQ5=makeQuery(id+"F0.imprint","IMPRINT",EDGE,{"disambiguationData":[TD([[makeQuery(id+"F0.imprint","INTERSECT",VERTEX,{"derivedFrom":[subQ3,subQ2]}),1.0]])],"derivedFrom":subQ3});var subQ7=makeQuery(id+"F0.imprint","IMPRINT",EDGE,{"disambiguationData":[TD([[subQ4,1.0]])],"derivedFrom":subQ3});var subQ8=sQuery(id+"F0.wireOp",EDGE,"E1");var subQ9=makeQuery(id+"F0.imprint","IMPRINT",EDGE,{"disambiguationData":[TD([[makeQuery(id+"F0.imprint","INTERSECT",VERTEX,{"disambiguationData":[OD(0.0)],"derivedFrom":[subQ8,subQ3]}),-1.0]])],"derivedFrom":subQ3});Q15=makeQuery(id+"F6.boolean.opBoolean","SPLIT",EDGE,{"disambiguationData":[TD([makeQuery(id+"F1.opExtrude","CAP_FACE",FACE,{"disambiguationData":[OSD([sQuery(id+"F0.wireOp",EDGE,"E0.bottom"),subQ8,sQuery(id+"F0.wireOp",EDGE,"E2.bottom"),sQuery(id+"F0.wireOp",EDGE,"E2.left"),sQuery(id+"F0.wireOp",EDGE,"E2.right"),sQuery(id+"F0.wireOp",EDGE,"E15"),sQuery(id+"F0.wireOp",EDGE,"E18"),sQuery(id+"F0.wireOp",EDGE,"E19"),subQ3,subQ2,sQuery(id+"F0.wireOp",EDGE,"E59.MirrorCS"),sQuery(id+"F0.wireOp",EDGE,"E60.MirrorCS")])],"isStart":true}),makeQuery(id+"F1.opExtrude","SWEPT_FACE",FACE,{"disambiguationData":[OSD([subQ3]),TDD([subQ9,subQ7,subQ5])]}),makeQuery(id+"F1.opExtrude","SWEPT_FACE",FACE,{"disambiguationData":[OSD([subQ2])]}),makeQuery(id+"F6.opExtrude","CAP_FACE",FACE,{"disambiguationData":[OSD([sQuery(id+"F0.wireOp",EDGE,"E29.MirrorCS"),sQuery(id+"F0.wireOp",EDGE,"E30.MirrorCS"),sQuery(id+"F0.wireOp",EDGE,"E31.MirrorCS"),sQuery(id+"F0.wireOp",EDGE,"E46.MirrorCS"),subQ1,subQ0])],"isStart":true}),makeQuery(id+"F6.opExtrude","SWEPT_FACE",FACE,{"disambiguationData":[OSD([subQ0])]})])],"derivedFrom":makeQuery(id+"F1.opExtrude","CAP_EDGE",EDGE,{"disambiguationData":[OSD([subQ3]),TDD([subQ9,subQ7,subQ5])],"isStart":true})});}
            var Q16;
            {var subQ0=sQuery(id+"F0.wireOp",EDGE,"E1");var subQ1=sQuery(id+"F0.wireOp",EDGE,"E54.MirrorCS");var subQ3=sQuery(id+"F0.wireOp",EDGE,"E58.MirrorCS");var subQ4=sQuery(id+"F0.wireOp",EDGE,"E57.MirrorCS");var subQ5=makeQuery(id+"F0.imprint","INTERSECT",VERTEX,{"derivedFrom":[subQ1,subQ4]});var subQ6=makeQuery(id+"F0.imprint","IMPRINT",EDGE,{"disambiguationData":[TD([[makeQuery(id+"F0.imprint","INTERSECT",VERTEX,{"derivedFrom":[subQ4,subQ3]}),1.0]])],"derivedFrom":subQ4});var subQ8=makeQuery(id+"F0.imprint","IMPRINT",EDGE,{"disambiguationData":[TD([[subQ5,1.0]])],"derivedFrom":subQ4});var subQ9=makeQuery(id+"F0.imprint","IMPRINT",EDGE,{"disambiguationData":[TD([[makeQuery(id+"F0.imprint","INTERSECT",VERTEX,{"disambiguationData":[OD(0.0)],"derivedFrom":[subQ0,subQ4]}),-1.0]])],"derivedFrom":subQ4});var subQ10=makeQuery(id+"F1.opExtrude","SWEPT_FACE",FACE,{"disambiguationData":[OSD([subQ4]),TDD([subQ9,subQ8,subQ6])]});var subQ11=makeQuery(id+"F1.opExtrude","CAP_FACE",FACE,{"disambiguationData":[OSD([sQuery(id+"F0.wireOp",EDGE,"E0.bottom"),subQ0,sQuery(id+"F0.wireOp",EDGE,"E2.bottom"),sQuery(id+"F0.wireOp",EDGE,"E2.left"),sQuery(id+"F0.wireOp",EDGE,"E2.right"),sQuery(id+"F0.wireOp",EDGE,"E15"),sQuery(id+"F0.wireOp",EDGE,"E18"),sQuery(id+"F0.wireOp",EDGE,"E19"),subQ4,subQ3,sQuery(id+"F0.wireOp",EDGE,"E59.MirrorCS"),sQuery(id+"F0.wireOp",EDGE,"E60.MirrorCS")])],"isStart":true});Q16=makeQuery(id+"F6.boolean.opBoolean","SPLIT",EDGE,{"disambiguationData":[topologyDisambiguationEdgeConnected([subQ11,subQ10]),TD([makeQuery(id+"F2.opExtrude","SWEPT_FACE",FACE,{"disambiguationData":[OSD([subQ0])]})])],"derivedFrom":makeQuery(id+"F1.opExtrude","CAP_EDGE",EDGE,{"disambiguationData":[OSD([subQ4]),TDD([subQ9,subQ8,subQ6])],"isStart":true})});}
            var Q17;
            {var subQ0=sQuery(id+"F0.wireOp",EDGE,"E20.top");var subQ2=sQuery(id+"F0.wireOp",EDGE,"E1");var subQ3=sQuery(id+"F0.wireOp",EDGE,"E19");var subQ4=sQuery(id+"F0.wireOp",EDGE,"E15");var subQ5=makeQuery(id+"F0.imprint","INTERSECT",VERTEX,{"derivedFrom":[subQ3,subQ0]});var subQ6=makeQuery(id+"F0.imprint","IMPRINT",EDGE,{"disambiguationData":[TD([[makeQuery(id+"F0.imprint","INTERSECT",VERTEX,{"derivedFrom":[subQ4,subQ3]}),1.0]])],"derivedFrom":subQ3});var subQ8=makeQuery(id+"F0.imprint","IMPRINT",EDGE,{"disambiguationData":[TD([[subQ5,1.0]])],"derivedFrom":subQ3});var subQ9=makeQuery(id+"F0.imprint","IMPRINT",EDGE,{"disambiguationData":[TD([[makeQuery(id+"F0.imprint","INTERSECT",VERTEX,{"disambiguationData":[OD(0.0)],"derivedFrom":[subQ2,subQ3]}),-1.0]])],"derivedFrom":subQ3});var subQ10=makeQuery(id+"F1.opExtrude","SWEPT_FACE",FACE,{"disambiguationData":[OSD([subQ3]),TDD([subQ9,subQ8,subQ6])]});var subQ11=makeQuery(id+"F1.opExtrude","CAP_FACE",FACE,{"disambiguationData":[OSD([sQuery(id+"F0.wireOp",EDGE,"E0.bottom"),subQ2,sQuery(id+"F0.wireOp",EDGE,"E2.bottom"),sQuery(id+"F0.wireOp",EDGE,"E2.left"),sQuery(id+"F0.wireOp",EDGE,"E2.right"),subQ4,sQuery(id+"F0.wireOp",EDGE,"E18"),subQ3,sQuery(id+"F0.wireOp",EDGE,"E57.MirrorCS"),sQuery(id+"F0.wireOp",EDGE,"E58.MirrorCS"),sQuery(id+"F0.wireOp",EDGE,"E59.MirrorCS"),sQuery(id+"F0.wireOp",EDGE,"E60.MirrorCS")])],"isStart":true});Q17=makeQuery(id+"F6.boolean.opBoolean","SPLIT",EDGE,{"disambiguationData":[topologyDisambiguationEdgeConnected([subQ11,subQ10]),TD([makeQuery(id+"F2.opExtrude","SWEPT_FACE",FACE,{"disambiguationData":[OSD([subQ2])]})])],"derivedFrom":makeQuery(id+"F1.opExtrude","CAP_EDGE",EDGE,{"disambiguationData":[OSD([subQ3]),TDD([subQ9,subQ8,subQ6])],"isStart":true})});}
            var Q18;
            {var subQ0=sQuery(id+"F0.wireOp",EDGE,"E20.top");var subQ1=sQuery(id+"F0.wireOp",EDGE,"E20.bottom");var subQ2=sQuery(id+"F0.wireOp",EDGE,"E15");var subQ3=sQuery(id+"F0.wireOp",EDGE,"E19");var subQ4=makeQuery(id+"F0.imprint","INTERSECT",VERTEX,{"derivedFrom":[subQ3,subQ0]});var subQ5=makeQuery(id+"F0.imprint","IMPRINT",EDGE,{"disambiguationData":[TD([[makeQuery(id+"F0.imprint","INTERSECT",VERTEX,{"derivedFrom":[subQ2,subQ3]}),1.0]])],"derivedFrom":subQ3});var subQ7=makeQuery(id+"F0.imprint","IMPRINT",EDGE,{"disambiguationData":[TD([[subQ4,1.0]])],"derivedFrom":subQ3});var subQ8=sQuery(id+"F0.wireOp",EDGE,"E1");var subQ9=makeQuery(id+"F0.imprint","IMPRINT",EDGE,{"disambiguationData":[TD([[makeQuery(id+"F0.imprint","INTERSECT",VERTEX,{"disambiguationData":[OD(0.0)],"derivedFrom":[subQ8,subQ3]}),-1.0]])],"derivedFrom":subQ3});Q18=makeQuery(id+"F6.boolean.opBoolean","SPLIT",EDGE,{"disambiguationData":[TD([makeQuery(id+"F1.opExtrude","CAP_FACE",FACE,{"disambiguationData":[OSD([sQuery(id+"F0.wireOp",EDGE,"E0.bottom"),subQ8,sQuery(id+"F0.wireOp",EDGE,"E2.bottom"),sQuery(id+"F0.wireOp",EDGE,"E2.left"),sQuery(id+"F0.wireOp",EDGE,"E2.right"),subQ2,sQuery(id+"F0.wireOp",EDGE,"E18"),subQ3,sQuery(id+"F0.wireOp",EDGE,"E57.MirrorCS"),sQuery(id+"F0.wireOp",EDGE,"E58.MirrorCS"),sQuery(id+"F0.wireOp",EDGE,"E59.MirrorCS"),sQuery(id+"F0.wireOp",EDGE,"E60.MirrorCS")])],"isStart":true}),makeQuery(id+"F1.opExtrude","SWEPT_FACE",FACE,{"disambiguationData":[OSD([subQ2])]}),makeQuery(id+"F1.opExtrude","SWEPT_FACE",FACE,{"disambiguationData":[OSD([subQ3]),TDD([subQ9,subQ7,subQ5])]}),makeQuery(id+"F6.opExtrude","CAP_FACE",FACE,{"disambiguationData":[OSD([sQuery(id+"F0.wireOp",EDGE,"E5.1"),subQ1,subQ0,sQuery(id+"F0.wireOp",EDGE,"E20.right"),sQuery(id+"F0.wireOp",EDGE,"E21.filletArc"),sQuery(id+"F0.wireOp",EDGE,"E22.filletArc")])],"isStart":true}),makeQuery(id+"F6.opExtrude","SWEPT_FACE",FACE,{"disambiguationData":[OSD([subQ0])]})])],"derivedFrom":makeQuery(id+"F1.opExtrude","CAP_EDGE",EDGE,{"disambiguationData":[OSD([subQ3]),TDD([subQ9,subQ7,subQ5])],"isStart":true})});}
            var Q19;
            Q19=makeQuery(id+"F1.opExtrude","CAP_EDGE",EDGE,{"disambiguationData":[OSD([sQuery(id+"F0.wireOp",EDGE,"E15")])],"isStart":true});
            var Q20;
            Q20=makeQuery(id+"F1.opExtrude","CAP_EDGE",EDGE,{"disambiguationData":[OSD([sQuery(id+"F0.wireOp",EDGE,"E18")])],"isStart":true});
            var Q21;
            Q21=makeQuery(id+"F1.opExtrude","SWEPT_EDGE",EDGE,{"disambiguationData":[OSD([sQuery(id+"F0.wireOp",EDGE,"E59.MirrorCS"),sQuery(id+"F0.wireOp",EDGE,"E60.MirrorCS")])]});
            var Q22;
            Q22=makeQuery(id+"F1.opExtrude","SWEPT_EDGE",EDGE,{"disambiguationData":[OSD([sQuery(id+"F0.wireOp",EDGE,"E0.bottom"),sQuery(id+"F0.wireOp",EDGE,"E18")])]});
            var Q23;
            Q23=makeQuery(id+"F1.opExtrude","CAP_EDGE",EDGE,{"disambiguationData":[OSD([sQuery(id+"F0.wireOp",EDGE,"E0.bottom"),sQuery(id+"F0.wireOp",EDGE,"E59.MirrorCS")])],"isStart":false});
            var Q24;
            Q24=makeQuery(id+"F1.opExtrude","CAP_EDGE",EDGE,{"disambiguationData":[OSD([sQuery(id+"F0.wireOp",EDGE,"E18")])],"isStart":false});
            var Q25;
            {var subQ0=sQuery(id+"F0.wireOp",EDGE,"E19");var subQ1=makeQuery(id+"F0.imprint","INTERSECT",VERTEX,{"derivedFrom":[subQ0,sQuery(id+"F0.wireOp",EDGE,"E20.top")]});Q25=makeQuery(id+"F1.opExtrude","CAP_EDGE",EDGE,{"disambiguationData":[OSD([subQ0]),TDD([makeQuery(id+"F0.imprint","IMPRINT",EDGE,{"disambiguationData":[TD([[makeQuery(id+"F0.imprint","INTERSECT",VERTEX,{"disambiguationData":[OD(0.0)],"derivedFrom":[sQuery(id+"F0.wireOp",EDGE,"E1"),subQ0]}),-1.0]])],"derivedFrom":subQ0}),makeQuery(id+"F0.imprint","IMPRINT",EDGE,{"disambiguationData":[TD([[subQ1,1.0]])],"derivedFrom":subQ0}),makeQuery(id+"F0.imprint","IMPRINT",EDGE,{"disambiguationData":[TD([[makeQuery(id+"F0.imprint","INTERSECT",VERTEX,{"derivedFrom":[sQuery(id+"F0.wireOp",EDGE,"E15"),subQ0]}),1.0]])],"derivedFrom":subQ0})])],"isStart":false});}
            var Q26;
            {var subQ0=sQuery(id+"F0.wireOp",EDGE,"E19");var subQ4=sQuery(id+"F0.wireOp",EDGE,"E1");var subQ6=makeQuery(id+"F0.imprint","INTERSECT",VERTEX,{"derivedFrom":[sQuery(id+"F0.wireOp",EDGE,"E12.bottom"),subQ0]});var subQ7=sQuery(id+"F0.wireOp",EDGE,"E11.top");Q26=makeQuery(id+"F2.boolean.opBoolean","SPLIT",EDGE,{"disambiguationData":[TD([makeQuery(id+"F1.opExtrude","SWEPT_FACE",FACE,{"disambiguationData":[OSD([subQ0]),TDD([makeQuery(id+"F0.imprint","IMPRINT",EDGE,{"disambiguationData":[TD([[makeQuery(id+"F0.imprint","INTERSECT",VERTEX,{"derivedFrom":[subQ7,subQ0]}),-1.0]])],"derivedFrom":subQ0}),makeQuery(id+"F0.imprint","IMPRINT",EDGE,{"disambiguationData":[TD([[subQ6,-1.0]])],"derivedFrom":subQ0}),makeQuery(id+"F0.imprint","IMPRINT",EDGE,{"disambiguationData":[TD([[makeQuery(id+"F0.imprint","INTERSECT",VERTEX,{"disambiguationData":[OD(1.0)],"derivedFrom":[subQ4,subQ0]}),1.0]])],"derivedFrom":subQ0})])]})])],"derivedFrom":makeQuery(id+"F2.opExtrude","CAP_EDGE",EDGE,{"disambiguationData":[OSD([subQ4])],"isStart":true})});}
            var Q27;
            {var subQ0=sQuery(id+"F0.wireOp",EDGE,"E19");var subQ2=makeQuery(id+"F0.imprint","INTERSECT",VERTEX,{"derivedFrom":[sQuery(id+"F0.wireOp",EDGE,"E12.bottom"),subQ0]});Q27=makeQuery(id+"F1.opExtrude","CAP_EDGE",EDGE,{"disambiguationData":[OSD([subQ0]),TDD([makeQuery(id+"F0.imprint","IMPRINT",EDGE,{"disambiguationData":[TD([[makeQuery(id+"F0.imprint","INTERSECT",VERTEX,{"derivedFrom":[sQuery(id+"F0.wireOp",EDGE,"E11.top"),subQ0]}),-1.0]])],"derivedFrom":subQ0}),makeQuery(id+"F0.imprint","IMPRINT",EDGE,{"disambiguationData":[TD([[subQ2,-1.0]])],"derivedFrom":subQ0}),makeQuery(id+"F0.imprint","IMPRINT",EDGE,{"disambiguationData":[TD([[makeQuery(id+"F0.imprint","INTERSECT",VERTEX,{"disambiguationData":[OD(1.0)],"derivedFrom":[sQuery(id+"F0.wireOp",EDGE,"E1"),subQ0]}),1.0]])],"derivedFrom":subQ0})])],"isStart":false});}
            var Q28;
            {var subQ0=sQuery(id+"F0.wireOp",EDGE,"E57.MirrorCS");var subQ2=makeQuery(id+"F0.imprint","INTERSECT",VERTEX,{"derivedFrom":[sQuery(id+"F0.wireOp",EDGE,"E45.MirrorCS"),subQ0]});Q28=makeQuery(id+"F1.opExtrude","CAP_EDGE",EDGE,{"disambiguationData":[OSD([subQ0]),TDD([makeQuery(id+"F0.imprint","IMPRINT",EDGE,{"disambiguationData":[TD([[makeQuery(id+"F0.imprint","INTERSECT",VERTEX,{"derivedFrom":[sQuery(id+"F0.wireOp",EDGE,"E56.MirrorCS"),subQ0]}),-1.0]])],"derivedFrom":subQ0}),makeQuery(id+"F0.imprint","IMPRINT",EDGE,{"disambiguationData":[TD([[subQ2,-1.0]])],"derivedFrom":subQ0}),makeQuery(id+"F0.imprint","IMPRINT",EDGE,{"disambiguationData":[TD([[makeQuery(id+"F0.imprint","INTERSECT",VERTEX,{"disambiguationData":[OD(1.0)],"derivedFrom":[sQuery(id+"F0.wireOp",EDGE,"E1"),subQ0]}),1.0]])],"derivedFrom":subQ0})])],"isStart":false});}
            var Q29;
            {var subQ1=sQuery(id+"F0.wireOp",EDGE,"E57.MirrorCS");var subQ4=sQuery(id+"F0.wireOp",EDGE,"E1");var subQ5=sQuery(id+"F0.wireOp",EDGE,"E56.MirrorCS");var subQ8=makeQuery(id+"F0.imprint","INTERSECT",VERTEX,{"derivedFrom":[sQuery(id+"F0.wireOp",EDGE,"E45.MirrorCS"),subQ1]});Q29=makeQuery(id+"F2.boolean.opBoolean","SPLIT",EDGE,{"disambiguationData":[TD([makeQuery(id+"F1.opExtrude","SWEPT_FACE",FACE,{"disambiguationData":[OSD([subQ1]),TDD([makeQuery(id+"F0.imprint","IMPRINT",EDGE,{"disambiguationData":[TD([[makeQuery(id+"F0.imprint","INTERSECT",VERTEX,{"derivedFrom":[subQ5,subQ1]}),-1.0]])],"derivedFrom":subQ1}),makeQuery(id+"F0.imprint","IMPRINT",EDGE,{"disambiguationData":[TD([[subQ8,-1.0]])],"derivedFrom":subQ1}),makeQuery(id+"F0.imprint","IMPRINT",EDGE,{"disambiguationData":[TD([[makeQuery(id+"F0.imprint","INTERSECT",VERTEX,{"disambiguationData":[OD(1.0)],"derivedFrom":[subQ4,subQ1]}),1.0]])],"derivedFrom":subQ1})])]})])],"derivedFrom":makeQuery(id+"F2.opExtrude","CAP_EDGE",EDGE,{"disambiguationData":[OSD([subQ4])],"isStart":true})});}
            var Q30;
            {var subQ0=sQuery(id+"F0.wireOp",EDGE,"E57.MirrorCS");var subQ1=makeQuery(id+"F0.imprint","INTERSECT",VERTEX,{"derivedFrom":[sQuery(id+"F0.wireOp",EDGE,"E54.MirrorCS"),subQ0]});Q30=makeQuery(id+"F1.opExtrude","CAP_EDGE",EDGE,{"disambiguationData":[OSD([subQ0]),TDD([makeQuery(id+"F0.imprint","IMPRINT",EDGE,{"disambiguationData":[TD([[makeQuery(id+"F0.imprint","INTERSECT",VERTEX,{"disambiguationData":[OD(0.0)],"derivedFrom":[sQuery(id+"F0.wireOp",EDGE,"E1"),subQ0]}),-1.0]])],"derivedFrom":subQ0}),makeQuery(id+"F0.imprint","IMPRINT",EDGE,{"disambiguationData":[TD([[subQ1,1.0]])],"derivedFrom":subQ0}),makeQuery(id+"F0.imprint","IMPRINT",EDGE,{"disambiguationData":[TD([[makeQuery(id+"F0.imprint","INTERSECT",VERTEX,{"derivedFrom":[subQ0,sQuery(id+"F0.wireOp",EDGE,"E58.MirrorCS")]}),1.0]])],"derivedFrom":subQ0})])],"isStart":false});}
            var Q31;
            Q31=makeQuery(id+"F1.opExtrude","CAP_EDGE",EDGE,{"disambiguationData":[OSD([sQuery(id+"F0.wireOp",EDGE,"E58.MirrorCS")])],"isStart":false});
            var Q32;
            Q32=makeQuery(id+"F1.opExtrude","CAP_EDGE",EDGE,{"disambiguationData":[OSD([sQuery(id+"F0.wireOp",EDGE,"E60.MirrorCS")])],"isStart":false});
            fillet(context, id + "F9", {"entities" : qUnion([Q0, Q1, Q2, Q3, Q4, Q5, Q6, Q7, Q8, Q9, Q10, Q11, Q12, Q13, Q14, Q15, Q16, Q17, Q18, Q19, Q20, Q21, Q22, Q23, Q24, Q25, Q26, Q27, Q28, Q29, Q30, Q31, Q32]), "radius" : 1.45 * mm, "tangentPropagation" : true, "allowEdgeOverflow" : false});
        }
        {
            var Q0;
            Q0=qCreatedBy(makeId("Right.planeOp"),FACE);
            var sketch = newSketch(context, id + "F10", { "sketchPlane" : qUnion([Q0])});
            skCircle(sketch, "E61", {"center": v(36.4, -11.5) * mm, "radius": 13.85 * mm});
            skCircle(sketch, "E62", {"center": v(-10.1, -11.5) * mm, "radius": 13.85 * mm});
            skCircle(sketch, "E63", {"center": v(-55.85, -11.5) * mm, "radius": 13.85 * mm});
            skCircle(sketch, "E64", {"center": v(-55.85, -11.5) * mm, "radius": 1.75 * mm});
            skCircle(sketch, "E65", {"center": v(-10.1, -11.5) * mm, "radius": 1.75 * mm});
            skCircle(sketch, "E66", {"center": v(36.4, -11.5) * mm, "radius": 1.75 * mm});
            skSolve(sketch);
        }
        {
            var Q0;
            Q0=makeQuery(id+"F10.imprint","IMPRINT",FACE,{"disambiguationData":[TD([[makeQuery(id+"F10.imprint","IMPRINT",EDGE,{"derivedFrom":sQuery(id+"F10.wireOp",EDGE,"E61")}),1.0]])]});
            var Q1;
            Q1=makeQuery(id+"F10.imprint","IMPRINT",FACE,{"disambiguationData":[TD([[makeQuery(id+"F10.imprint","IMPRINT",EDGE,{"derivedFrom":sQuery(id+"F10.wireOp",EDGE,"E62")}),1.0]])]});
            var Q2;
            Q2=makeQuery(id+"F10.imprint","IMPRINT",FACE,{"disambiguationData":[TD([[makeQuery(id+"F10.imprint","IMPRINT",EDGE,{"derivedFrom":sQuery(id+"F10.wireOp",EDGE,"E63")}),1.0]])]});
            extrude(context, id + "F11", {"entities" : qUnion([Q0, Q1, Q2]), "depth" : 21 * mm, "hasSecondDirection" : true, "secondDirectionOppositeDirection" : false, "secondDirectionDepth" : 15.5 * mm});
        }
        {
            var Q0;
            Q0=makeQuery(id+"F10.imprint","IMPRINT",FACE,{"disambiguationData":[TD([[makeQuery(id+"F10.imprint","IMPRINT",EDGE,{"derivedFrom":sQuery(id+"F10.wireOp",EDGE,"E61")}),1.0]])]});
            var Q1;
            Q1=makeQuery(id+"F10.imprint","IMPRINT",FACE,{"disambiguationData":[TD([[makeQuery(id+"F10.imprint","IMPRINT",EDGE,{"derivedFrom":sQuery(id+"F10.wireOp",EDGE,"E62")}),1.0]])]});
            var Q2;
            Q2=makeQuery(id+"F10.imprint","IMPRINT",FACE,{"disambiguationData":[TD([[makeQuery(id+"F10.imprint","IMPRINT",EDGE,{"derivedFrom":sQuery(id+"F10.wireOp",EDGE,"E63")}),1.0]])]});
            extrude(context, id + "F12", {"entities" : qUnion([Q0, Q1, Q2]), "oppositeDirection" : true, "depth" : 20 * mm, "hasSecondDirection" : true, "secondDirectionOppositeDirection" : true, "secondDirectionDepth" : 15.5 * mm});
        }
        {
            var Q0;
            Q0=makeQuery(id+"F11.opExtrude","SWEPT_FACE",FACE,{"disambiguationData":[OSD([sQuery(id+"F10.wireOp",EDGE,"E61")])]});
            var Q1;
            Q1=makeQuery(id+"F11.opExtrude","SWEPT_FACE",FACE,{"disambiguationData":[OSD([sQuery(id+"F10.wireOp",EDGE,"E63")])]});
            var Q2;
            Q2=makeQuery(id+"F12.opExtrude","SWEPT_FACE",FACE,{"disambiguationData":[OSD([sQuery(id+"F10.wireOp",EDGE,"E63")])]});
            var Q3;
            Q3=makeQuery(id+"F12.opExtrude","SWEPT_FACE",FACE,{"disambiguationData":[OSD([sQuery(id+"F10.wireOp",EDGE,"E62")])]});
            var Q4;
            Q4=makeQuery(id+"F12.opExtrude","SWEPT_FACE",FACE,{"disambiguationData":[OSD([sQuery(id+"F10.wireOp",EDGE,"E61")])]});
            var Q5;
            Q5=makeQuery(id+"F11.opExtrude","SWEPT_FACE",FACE,{"disambiguationData":[OSD([sQuery(id+"F10.wireOp",EDGE,"E62")])]});
            fillet(context, id + "F13", {"entities" : qUnion([Q0, Q1, Q2, Q3, Q4, Q5]), "radius" : 1.2 * mm, "tangentPropagation" : true, "allowEdgeOverflow" : false});
        }
        {
            var Q0;
            Q0=makeQuery(id+"F10.imprint","IMPRINT",FACE,{"disambiguationData":[TD([[makeQuery(id+"F10.imprint","IMPRINT",EDGE,{"derivedFrom":sQuery(id+"F10.wireOp",EDGE,"E64")}),1.0]])]});
            var Q1;
            Q1=makeQuery(id+"F10.imprint","IMPRINT",FACE,{"disambiguationData":[TD([[makeQuery(id+"F10.imprint","IMPRINT",EDGE,{"derivedFrom":sQuery(id+"F10.wireOp",EDGE,"E65")}),1.0]])]});
            var Q2;
            Q2=makeQuery(id+"F10.imprint","IMPRINT",FACE,{"disambiguationData":[TD([[makeQuery(id+"F10.imprint","IMPRINT",EDGE,{"derivedFrom":sQuery(id+"F10.wireOp",EDGE,"E66")}),1.0]])]});
            var Q3;
            Q3=makeQuery(id+"F4.opExtrude","SWEPT_FACE",FACE,{"disambiguationData":[OSD([sQuery(id+"F0.wireOp",EDGE,"E5.1")])]});
            var Q4;
            Q4=makeQuery(id+"F4.opExtrude","SWEPT_FACE",FACE,{"disambiguationData":[OSD([sQuery(id+"F0.wireOp",EDGE,"E46.MirrorCS")])]});
            extrude(context, id + "F14", {"entities" : qUnion([Q0, Q1, Q2]), "operationType" : NewBodyOperationType.ADD, "endBound" : BoundingType.UP_TO_SURFACE, "oppositeDirection" : true, "endBoundEntityFace" : qUnion([Q3]), "depth" : 25 * mm, "hasSecondDirection" : true, "secondDirectionBound" : SecondDirectionBoundingType.UP_TO_SURFACE, "secondDirectionOppositeDirection" : false, "secondDirectionBoundEntityFace" : qUnion([Q4]), "secondDirectionDepth" : 25 * mm});
        }
        {
            var Q0;
            Q0=makeQuery(id+"F2.opExtrude","CAP_EDGE",EDGE,{"disambiguationData":[OSD([sQuery(id+"F0.wireOp",EDGE,"E1")])],"isStart":false});
            fillet(context, id + "F15", {"entities" : qUnion([Q0]), "radius" : 1.45 * mm, "tangentPropagation" : true, "allowEdgeOverflow" : false});
        }
    });
